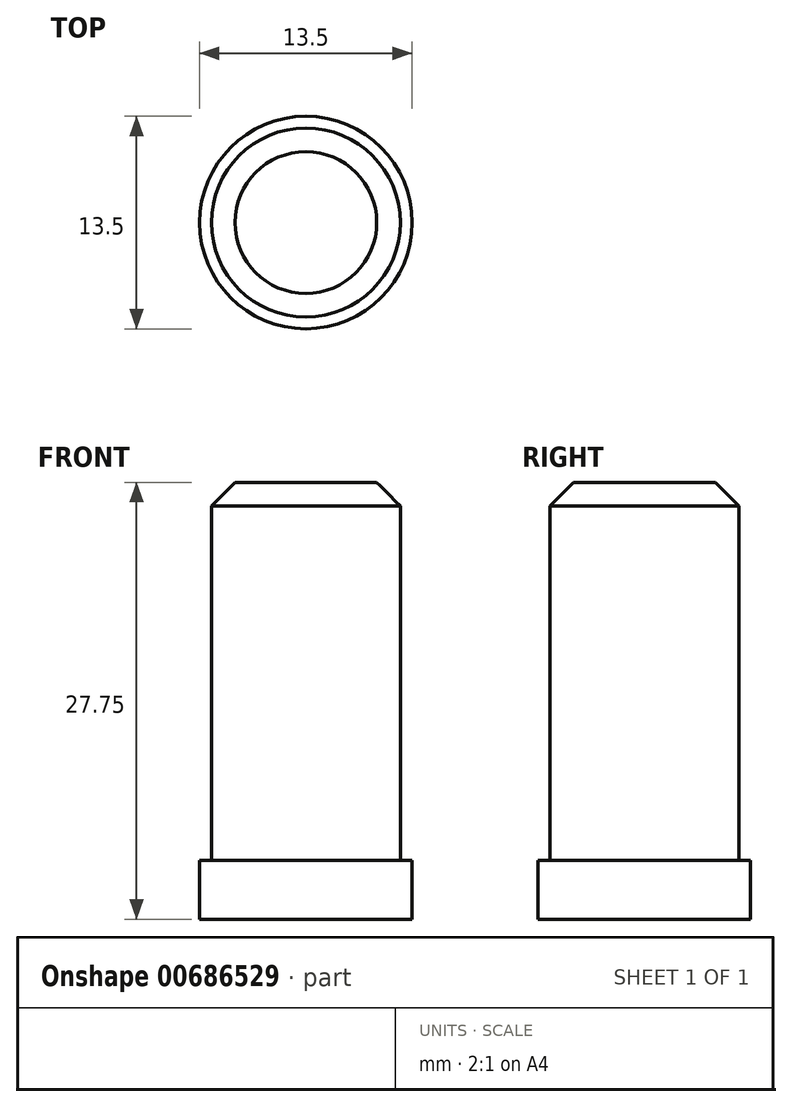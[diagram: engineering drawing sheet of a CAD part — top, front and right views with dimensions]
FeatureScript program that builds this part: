
annotation { "Feature Type Name" : "Feature", "Feature Type Description" : "" }
export const myFeature = defineFeature(function(context is Context, id is Id, definition is map)
    precondition{}
    {
        {
            var Q0;
            Q0=qCreatedBy(makeId("Front.planeOp"),FACE);
            var sketch = newSketch(context, id + "F0", { "sketchPlane" : qUnion([Q0])});
            skLineSegment(sketch, "E0.bottom", {"start": v(-4.5, 24) * mm, "end": v(0, 24) * mm});
            skLineSegment(sketch, "E0.top", {"start": v(-6, 22.5) * mm, "end": v(0, 22.5) * mm});
            skLineSegment(sketch, "E1.right", {"start": v(0, 22.5) * mm, "end": v(0, 0) * mm});
            skLineSegment(sketch, "E2.bottom", {"start": v(-6.75, 0) * mm, "end": v(0, 0) * mm});
            skLineSegment(sketch, "E2.top", {"start": v(-6.75, -3.75) * mm, "end": v(0, -3.75) * mm});
            skLineSegment(sketch, "E2.left", {"start": v(-6.75, 0) * mm, "end": v(-6.75, -3.75) * mm});
            skLineSegment(sketch, "E3", {"start": v(-6, 22.5) * mm, "end": v(-6, 0) * mm});
            skLineSegment(sketch, "E4", {"start": v(0, 0) * mm, "end": v(0, 22.5) * mm, "construction": true});
            skLineSegment(sketch, "E5", {"start": v(-6, 22.5) * mm, "end": v(-4.5, 24) * mm});
            skLineSegment(sketch, "E6", {"start": v(0, 22.5) * mm, "end": v(0, 24) * mm});
            skLineSegment(sketch, "E7", {"start": v(0, 27.55) * mm, "end": v(0, -7.85) * mm, "construction": true});
            skLineSegment(sketch, "E8", {"start": v(0, 0) * mm, "end": v(0, -3.75) * mm});
            skSolve(sketch);
        }
        {
            var Q0;
            Q0 = qSketchRegion(id + "F0", true);
            var Q1;
            Q1=sQuery(id+"F0.wireOp",EDGE,"E7");
            revolve(context, id + "F1", {"entities" : qUnion([Q0]), "axis" : qUnion([Q1]), "revolveType" : RevolveType.FULL});
        }
    });
